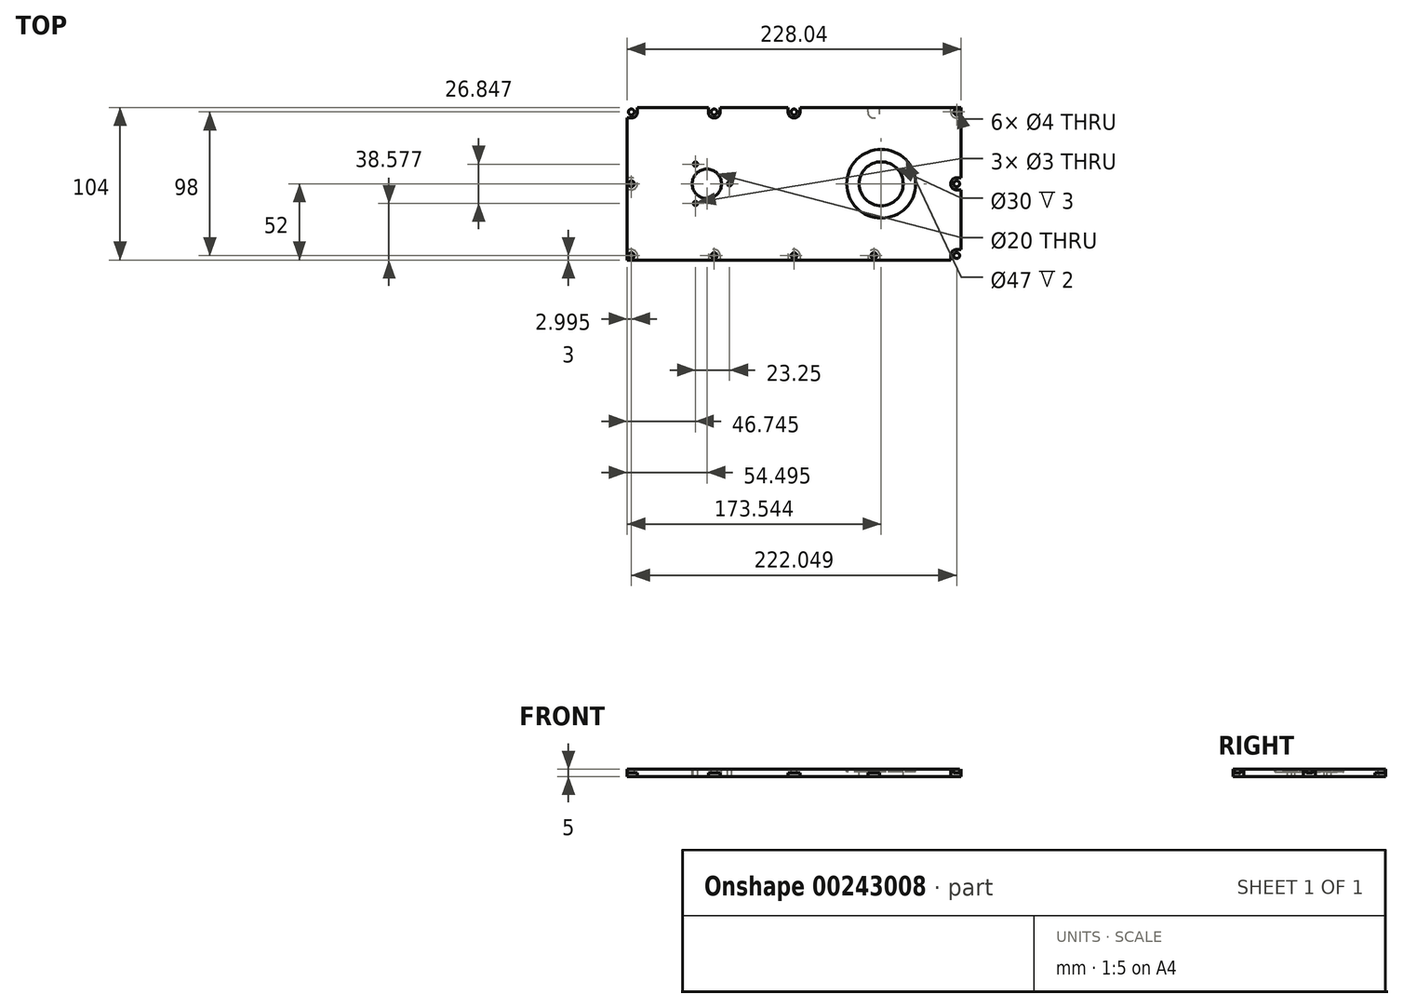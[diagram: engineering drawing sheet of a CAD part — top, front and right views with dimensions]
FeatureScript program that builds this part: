
annotation { "Feature Type Name" : "Feature", "Feature Type Description" : "" }
export const myFeature = defineFeature(function(context is Context, id is Id, definition is map)
    precondition{}
    {
        {
            var Q0;
            Q0=qCreatedBy(makeId("Top.planeOp"),FACE);
            var sketch = newSketch(context, id + "F0", { "sketchPlane" : qUnion([Q0])});
            skLineSegment(sketch, "E0.bottom", {"start": v(-114.02, 52) * mm, "end": v(114.02, 52) * mm});
            skLineSegment(sketch, "E0.top", {"start": v(-114.02, -52) * mm, "end": v(114.02, -52) * mm});
            skLineSegment(sketch, "E0.left", {"start": v(-114.02, 52) * mm, "end": v(-114.02, -52) * mm});
            skLineSegment(sketch, "E0.right", {"start": v(114.02, 52) * mm, "end": v(114.02, -52) * mm});
            skPoint(sketch, "E1", {"position": v(0, 52) * mm});
            skPoint(sketch, "E2", {"position": v(-114.02, 0) * mm});
            skPoint(sketch, "E3", {"position": v(59.52, 0) * mm});
            skCircle(sketch, "E4", {"center": v(-59.52, 0) * mm, "radius": 20.5 * mm, "construction": true});
            skCircle(sketch, "E5", {"center": v(-59.52, 0) * mm, "radius": 13.65 * mm});
            skCircle(sketch, "E6", {"center": v(59.52, 0) * mm, "radius": 23.5 * mm});
            skCircle(sketch, "E7", {"center": v(59.52, 0) * mm, "radius": 15 * mm});
            skCircle(sketch, "E8", {"center": v(-59.52, 0) * mm, "radius": 10 * mm});
            skCircle(sketch, "E9", {"center": v(-59.52, 0) * mm, "radius": 15.5 * mm, "construction": true});
            skCircle(sketch, "E10", {"center": v(-44.02, 0) * mm, "radius": 1.5 * mm});
            skCircle(sketch, "E11", {"center": v(-44.02, 0) * mm, "radius": 3.25 * mm, "construction": true});
            skCircle(sketch, "E12", {"center": v(-67.27, 13.42) * mm, "radius": 1.5 * mm});
            skCircle(sketch, "E13", {"center": v(-67.27, -13.42) * mm, "radius": 1.5 * mm});
            skCircle(sketch, "E14", {"center": v(-67.27, -13.42) * mm, "radius": 3.25 * mm, "construction": true});
            skCircle(sketch, "E15", {"center": v(-67.27, 13.42) * mm, "radius": 3.25 * mm, "construction": true});
            skLineSegment(sketch, "E16", {"start": v(-111.02, 69.97) * mm, "end": v(-111.02, -88.42) * mm, "construction": true});
            skLineSegment(sketch, "E17", {"start": v(-112.08, -49) * mm, "end": v(189.37, -49) * mm, "construction": true});
            skCircle(sketch, "E18", {"center": v(-111.02, 0) * mm, "radius": 2 * mm});
            skCircle(sketch, "E19", {"center": v(-111.02, -49) * mm, "radius": 2 * mm});
            skCircle(sketch, "E20", {"center": v(-54.5, -49) * mm, "radius": 2 * mm});
            skCircle(sketch, "E21", {"center": v(0, -49) * mm, "radius": 2 * mm});
            skCircle(sketch, "E22", {"center": v(54.5, -49) * mm, "radius": 2 * mm});
            skArc(sketch, "E23", {"start": v(58.38, -47.6) * mm, "mid": v(53.78, -44.94) * mm, "end": v(50.38, -49) * mm});
            skArc(sketch, "E24", {"start": v(4.12, -49) * mm, "mid": v(0, -44.88) * mm, "end": v(-4.12, -49) * mm});
            skArc(sketch, "E25", {"start": v(-50.38, -49) * mm, "mid": v(-54.5, -44.87) * mm, "end": v(-58.62, -49) * mm});
            skArc(sketch, "E26", {"start": v(-106.9, -49) * mm, "mid": v(-108.1, -46.08) * mm, "end": v(-111.02, -44.88) * mm});
            skArc(sketch, "E27", {"start": v(-111.02, -4.12) * mm, "mid": v(-106.9, 0) * mm, "end": v(-111.02, 4.12) * mm});
            skCircle(sketch, "E28.MirrorC", {"center": v(54.5, 49) * mm, "radius": 2 * mm});
            skCircle(sketch, "E29.MirrorC", {"center": v(0, 49) * mm, "radius": 2 * mm});
            skCircle(sketch, "E30.MirrorC", {"center": v(-54.5, 49) * mm, "radius": 2 * mm});
            skCircle(sketch, "E31.MirrorC", {"center": v(-111.02, 49) * mm, "radius": 2 * mm});
            skArc(sketch, "E32.MirrorC", {"start": v(-106.9, 49) * mm, "mid": v(-108.1, 46.08) * mm, "end": v(-111.02, 44.88) * mm});
            skArc(sketch, "E33.MirrorC", {"start": v(-50.38, 49) * mm, "mid": v(-53.78, 44.94) * mm, "end": v(-58.38, 47.6) * mm});
            skArc(sketch, "E34.MirrorC", {"start": v(4.12, 49) * mm, "mid": v(0, 44.88) * mm, "end": v(-4.12, 49) * mm});
            skArc(sketch, "E35.MirrorC", {"start": v(58.38, 47.6) * mm, "mid": v(53.78, 44.94) * mm, "end": v(50.38, 49) * mm});
            skCircle(sketch, "E36.MirrorC", {"center": v(111.02, 0) * mm, "radius": 2 * mm});
            skCircle(sketch, "E37.MirrorC", {"center": v(111.02, 49) * mm, "radius": 2 * mm});
            skArc(sketch, "E38.MirrorC", {"start": v(106.9, 49) * mm, "mid": v(108.1, 46.08) * mm, "end": v(111.02, 44.88) * mm});
            skPoint(sketch, "E39.MirrorP", {"position": v(114.02, 0) * mm});
            skArc(sketch, "E40.MirrorC", {"start": v(111.02, -4.12) * mm, "mid": v(106.9, 0) * mm, "end": v(111.02, 4.12) * mm});
            skCircle(sketch, "E41.MirrorC", {"center": v(111.02, -49) * mm, "radius": 2 * mm});
            skArc(sketch, "E42.MirrorC", {"start": v(106.9, -49) * mm, "mid": v(108.1, -46.08) * mm, "end": v(111.02, -44.88) * mm});
            skLineSegment(sketch, "E43", {"start": v(-111.02, 4.12) * mm, "end": v(-114.02, 4.12) * mm});
            skLineSegment(sketch, "E44", {"start": v(-111.02, -4.13) * mm, "end": v(-114.02, -4.13) * mm});
            skLineSegment(sketch, "E45", {"start": v(-106.9, -49) * mm, "end": v(-106.9, -52) * mm});
            skLineSegment(sketch, "E46", {"start": v(-111.02, -44.88) * mm, "end": v(-114.02, -44.88) * mm});
            skLineSegment(sketch, "E47", {"start": v(-58.38, -47.6) * mm, "end": v(-58.38, -52) * mm});
            skLineSegment(sketch, "E48", {"start": v(-50.38, -49) * mm, "end": v(-50.38, -52) * mm});
            skLineSegment(sketch, "E49", {"start": v(-4.13, -49) * mm, "end": v(-4.13, -52) * mm});
            skLineSegment(sketch, "E50", {"start": v(4.12, -49) * mm, "end": v(4.12, -52) * mm});
            skLineSegment(sketch, "E51.MirrorCS", {"start": v(-111.02, 44.88) * mm, "end": v(-114.02, 44.88) * mm});
            skLineSegment(sketch, "E52.MirrorCS", {"start": v(-106.9, 49) * mm, "end": v(-106.9, 52) * mm});
            skLineSegment(sketch, "E53.MirrorCS", {"start": v(-58.38, 47.6) * mm, "end": v(-58.38, 52) * mm});
            skLineSegment(sketch, "E54.MirrorCS", {"start": v(4.13, 49) * mm, "end": v(4.13, 52) * mm});
            skLineSegment(sketch, "E55.MirrorCS", {"start": v(-50.38, 49) * mm, "end": v(-50.38, 52) * mm});
            skLineSegment(sketch, "E56.MirrorCS", {"start": v(-4.13, 49) * mm, "end": v(-4.13, 52) * mm});
            skLineSegment(sketch, "E57.MirrorCS", {"start": v(106.9, 49) * mm, "end": v(106.9, 52) * mm});
            skLineSegment(sketch, "E58.MirrorCS", {"start": v(58.38, 47.6) * mm, "end": v(58.38, 52) * mm});
            skLineSegment(sketch, "E59.MirrorCS", {"start": v(50.38, 49) * mm, "end": v(50.38, 52) * mm});
            skArc(sketch, "E60.MirrorC", {"start": v(50.38, 49) * mm, "mid": v(53.78, 44.94) * mm, "end": v(58.38, 47.6) * mm});
            skLineSegment(sketch, "E61.MirrorCS", {"start": v(114.02, 52) * mm, "end": v(-114.02, 52) * mm});
            skLineSegment(sketch, "E62.MirrorCS", {"start": v(111.02, -44.88) * mm, "end": v(114.02, -44.88) * mm});
            skLineSegment(sketch, "E63.MirrorCS", {"start": v(111.02, -4.12) * mm, "end": v(114.02, -4.12) * mm});
            skLineSegment(sketch, "E64.MirrorCS", {"start": v(111.02, 44.88) * mm, "end": v(114.02, 44.88) * mm});
            skLineSegment(sketch, "E65.MirrorCS", {"start": v(111.02, 4.12) * mm, "end": v(114.02, 4.12) * mm});
            skLineSegment(sketch, "E66.MirrorCS", {"start": v(106.9, -49) * mm, "end": v(106.9, -52) * mm});
            skLineSegment(sketch, "E67.MirrorCS", {"start": v(58.38, -47.6) * mm, "end": v(58.38, -52) * mm});
            skLineSegment(sketch, "E68.MirrorCS", {"start": v(50.38, -49) * mm, "end": v(50.38, -52) * mm});
            skLineSegment(sketch, "E69", {"start": v(-67.27, 13.42) * mm, "end": v(-59.52, 0) * mm, "construction": true});
            skLineSegment(sketch, "E70", {"start": v(-67.27, -13.42) * mm, "end": v(-59.52, 0) * mm, "construction": true});
            skSolve(sketch);
        }
        {
            var Q0;
            Q0=makeQuery(id+"F0.imprint","IMPRINT",FACE,{"disambiguationData":[TD([[makeQuery(id+"F0.imprint","IMPRINT",EDGE,{"derivedFrom":sQuery(id+"F0.wireOp",EDGE,"E0.bottom")}),-1.0]])]});
            var Q1;
            Q1=makeQuery(id+"F0.imprint","IMPRINT",FACE,{"disambiguationData":[TD([[makeQuery(id+"F0.imprint","IMPRINT",EDGE,{"derivedFrom":sQuery(id+"F0.wireOp",EDGE,"E4")}),1.0]])]});
            var Q2;
            Q2=makeQuery(id+"F0.imprint","IMPRINT",FACE,{"disambiguationData":[TD([[makeQuery(id+"F0.imprint","IMPRINT",EDGE,{"derivedFrom":sQuery(id+"F0.wireOp",EDGE,"E6")}),1.0]])]});
            var Q3;
            Q3=makeQuery(id+"F0.imprint","IMPRINT",FACE,{"disambiguationData":[TD([[makeQuery(id+"F0.imprint","IMPRINT",EDGE,{"derivedFrom":sQuery(id+"F0.wireOp",EDGE,"E5")}),1.0]])]});
            var Q4;
            Q4=makeQuery(id+"F0.imprint","IMPRINT",FACE,{"disambiguationData":[TD([[makeQuery(id+"F0.imprint","IMPRINT",EDGE,{"derivedFrom":sQuery(id+"F0.wireOp",EDGE,"E5")}),-1.0]])]});
            extrude(context, id + "F1", {"entities" : qUnion([Q0, Q1, Q2, Q3, Q4]), "oppositeDirection" : true, "depth" : 5 * mm});
        }
        {
            var Q0;
            Q0=makeQuery(id+"F0.imprint","IMPRINT",FACE,{"disambiguationData":[TD([[makeQuery(id+"F0.imprint","IMPRINT",EDGE,{"derivedFrom":sQuery(id+"F0.wireOp",EDGE,"E6")}),1.0]])]});
            extrude(context, id + "F2", {"entities" : qUnion([Q0]), "operationType" : NewBodyOperationType.REMOVE, "oppositeDirection" : true, "depth" : 2 * mm});
        }
        {
            var Q0;
            Q0=makeQuery(id+"F0.imprint","IMPRINT",FACE,{"disambiguationData":[TD([[makeQuery(id+"F0.imprint","IMPRINT",EDGE,{"derivedFrom":sQuery(id+"F0.wireOp",EDGE,"E31.MirrorC")}),1.0]])]});
            var Q1;
            Q1=makeQuery(id+"F0.imprint","IMPRINT",FACE,{"disambiguationData":[TD([[makeQuery(id+"F0.imprint","IMPRINT",EDGE,{"derivedFrom":sQuery(id+"F0.wireOp",EDGE,"E18")}),-1.0]])]});
            var Q2;
            Q2=makeQuery(id+"F0.imprint","IMPRINT",FACE,{"disambiguationData":[TD([[makeQuery(id+"F0.imprint","IMPRINT",EDGE,{"derivedFrom":sQuery(id+"F0.wireOp",EDGE,"E19")}),-1.0]])]});
            var Q3;
            Q3=makeQuery(id+"F0.imprint","IMPRINT",FACE,{"disambiguationData":[TD([[makeQuery(id+"F0.imprint","IMPRINT",EDGE,{"derivedFrom":sQuery(id+"F0.wireOp",EDGE,"E20")}),-1.0]])]});
            var Q4;
            Q4=makeQuery(id+"F0.imprint","IMPRINT",FACE,{"disambiguationData":[TD([[makeQuery(id+"F0.imprint","IMPRINT",EDGE,{"derivedFrom":sQuery(id+"F0.wireOp",EDGE,"E21")}),-1.0]])]});
            var Q5;
            Q5=makeQuery(id+"F0.imprint","IMPRINT",FACE,{"disambiguationData":[TD([[makeQuery(id+"F0.imprint","IMPRINT",EDGE,{"derivedFrom":sQuery(id+"F0.wireOp",EDGE,"E22")}),-1.0]])]});
            var Q6;
            Q6=makeQuery(id+"F0.imprint","IMPRINT",FACE,{"disambiguationData":[TD([[makeQuery(id+"F0.imprint","IMPRINT",EDGE,{"derivedFrom":sQuery(id+"F0.wireOp",EDGE,"E41.MirrorC")}),1.0]])]});
            var Q7;
            Q7=makeQuery(id+"F0.imprint","IMPRINT",FACE,{"disambiguationData":[TD([[makeQuery(id+"F0.imprint","IMPRINT",EDGE,{"derivedFrom":sQuery(id+"F0.wireOp",EDGE,"E36.MirrorC")}),1.0]])]});
            var Q8;
            Q8=makeQuery(id+"F0.imprint","IMPRINT",FACE,{"disambiguationData":[TD([[makeQuery(id+"F0.imprint","IMPRINT",EDGE,{"derivedFrom":sQuery(id+"F0.wireOp",EDGE,"E37.MirrorC")}),-1.0]])]});
            var Q9;
            Q9=makeQuery(id+"F0.imprint","IMPRINT",FACE,{"disambiguationData":[TD([[makeQuery(id+"F0.imprint","IMPRINT",EDGE,{"derivedFrom":sQuery(id+"F0.wireOp",EDGE,"E28.MirrorC")}),1.0]])]});
            var Q10;
            Q10=makeQuery(id+"F0.imprint","IMPRINT",FACE,{"disambiguationData":[TD([[makeQuery(id+"F0.imprint","IMPRINT",EDGE,{"derivedFrom":sQuery(id+"F0.wireOp",EDGE,"E29.MirrorC")}),1.0]])]});
            var Q11;
            Q11=makeQuery(id+"F0.imprint","IMPRINT",FACE,{"disambiguationData":[TD([[makeQuery(id+"F0.imprint","IMPRINT",EDGE,{"derivedFrom":sQuery(id+"F0.wireOp",EDGE,"E30.MirrorC")}),1.0]])]});
            var Q12;
            {var subQ1=sQuery(id+"F0.wireOp",EDGE,"E58.MirrorCS");Q12=makeQuery(id+"F0.imprint","IMPRINT",FACE,{"disambiguationData":[TD([[makeQuery(id+"F0.imprint","IMPRINT",EDGE,{"derivedFrom":subQ1}),1.0]])]});}
            extrude(context, id + "F3", {"entities" : qUnion([Q0, Q1, Q2, Q3, Q4, Q5, Q6, Q7, Q8, Q9, Q10, Q11, Q12]), "operationType" : NewBodyOperationType.ADD, "oppositeDirection" : true, "depth" : 2.5 * mm});
        }
    });
